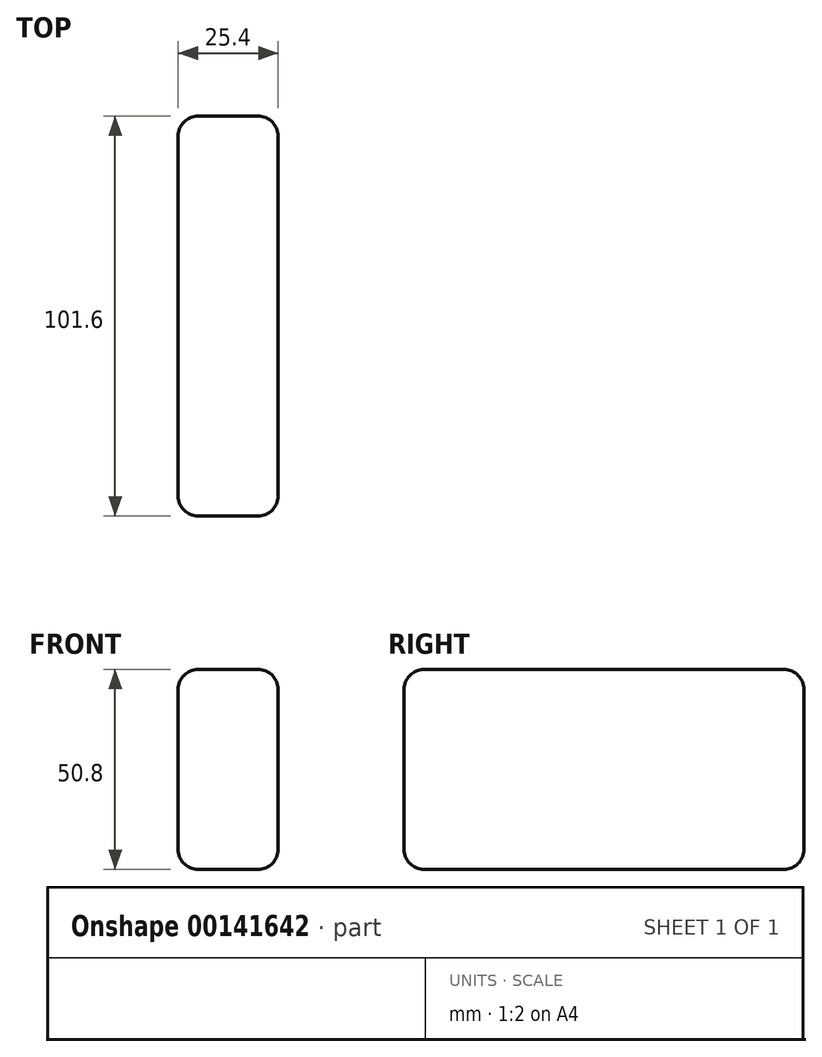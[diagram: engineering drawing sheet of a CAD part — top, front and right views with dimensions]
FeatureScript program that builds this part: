
annotation { "Feature Type Name" : "Feature", "Feature Type Description" : "" }
export const myFeature = defineFeature(function(context is Context, id is Id, definition is map)
    precondition{}
    {
        {
            var Q0;
            Q0=qCreatedBy(makeId("Front.planeOp"),FACE);
            var sketch = newSketch(context, id + "F0", { "sketchPlane" : qUnion([Q0])});
            skLineSegment(sketch, "E0.bottom", {"start": v(0, 0) * mm, "end": v(-25.4, 0) * mm});
            skLineSegment(sketch, "E0.top", {"start": v(0, 50.8) * mm, "end": v(-25.4, 50.8) * mm});
            skLineSegment(sketch, "E0.left", {"start": v(0, 0) * mm, "end": v(0, 50.8) * mm});
            skLineSegment(sketch, "E0.right", {"start": v(-25.4, 0) * mm, "end": v(-25.4, 50.8) * mm});
            skSolve(sketch);
        }
        {
            var Q0;
            Q0=makeQuery(id+"F0.imprint","IMPRINT",FACE,{"disambiguationData":[TD([[makeQuery(id+"F0.imprint","IMPRINT",EDGE,{"derivedFrom":sQuery(id+"F0.wireOp",EDGE,"E0.bottom")}),-1.0]])]});
            extrude(context, id + "F1", {"entities" : qUnion([Q0]), "oppositeDirection" : true, "depth" : 101.6 * mm});
        }
        {
            var Q0;
            Q0=makeQuery(id+"F1.opExtrude","CAP_EDGE",EDGE,{"disambiguationData":[OSD([sQuery(id+"F0.wireOp",EDGE,"E0.left")])],"isStart":true});
            var Q1;
            Q1=makeQuery(id+"F1.opExtrude","CAP_EDGE",EDGE,{"disambiguationData":[OSD([sQuery(id+"F0.wireOp",EDGE,"E0.right")])],"isStart":true});
            var Q2;
            Q2=makeQuery(id+"F1.opExtrude","CAP_EDGE",EDGE,{"disambiguationData":[OSD([sQuery(id+"F0.wireOp",EDGE,"E0.bottom")])],"isStart":true});
            var Q3;
            Q3=makeQuery(id+"F1.opExtrude","SWEPT_EDGE",EDGE,{"disambiguationData":[OSD([sQuery(id+"F0.wireOp",EDGE,"E0.bottom"),sQuery(id+"F0.wireOp",EDGE,"E0.left")])]});
            var Q4;
            Q4=makeQuery(id+"F1.opExtrude","CAP_EDGE",EDGE,{"disambiguationData":[OSD([sQuery(id+"F0.wireOp",EDGE,"E0.top")])],"isStart":true});
            var Q5;
            Q5=makeQuery(id+"F1.opExtrude","SWEPT_EDGE",EDGE,{"disambiguationData":[OSD([sQuery(id+"F0.wireOp",EDGE,"E0.top"),sQuery(id+"F0.wireOp",EDGE,"E0.left")])]});
            var Q6;
            Q6=makeQuery(id+"F1.opExtrude","SWEPT_EDGE",EDGE,{"disambiguationData":[OSD([sQuery(id+"F0.wireOp",EDGE,"E0.top"),sQuery(id+"F0.wireOp",EDGE,"E0.right")])]});
            var Q7;
            Q7=makeQuery(id+"F1.opExtrude","SWEPT_EDGE",EDGE,{"disambiguationData":[OSD([sQuery(id+"F0.wireOp",EDGE,"E0.bottom"),sQuery(id+"F0.wireOp",EDGE,"E0.right")])]});
            var Q8;
            Q8=makeQuery(id+"F1.opExtrude","CAP_EDGE",EDGE,{"disambiguationData":[OSD([sQuery(id+"F0.wireOp",EDGE,"E0.right")])],"isStart":false});
            var Q9;
            Q9=makeQuery(id+"F1.opExtrude","CAP_EDGE",EDGE,{"disambiguationData":[OSD([sQuery(id+"F0.wireOp",EDGE,"E0.left")])],"isStart":false});
            var Q10;
            Q10=makeQuery(id+"F1.opExtrude","CAP_EDGE",EDGE,{"disambiguationData":[OSD([sQuery(id+"F0.wireOp",EDGE,"E0.bottom")])],"isStart":false});
            var Q11;
            Q11=makeQuery(id+"F1.opExtrude","CAP_EDGE",EDGE,{"disambiguationData":[OSD([sQuery(id+"F0.wireOp",EDGE,"E0.top")])],"isStart":false});
            fillet(context, id + "F2", {"entities" : qUnion([Q0, Q1, Q2, Q3, Q4, Q5, Q6, Q7, Q8, Q9, Q10, Q11]), "radius" : 5.08 * mm, "tangentPropagation" : true, "allowEdgeOverflow" : false});
        }
    });
